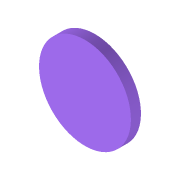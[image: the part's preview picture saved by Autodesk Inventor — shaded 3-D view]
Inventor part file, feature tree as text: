
AUTODESK INVENTOR PART (.ipt)
format: ipt  version: 2022 (Build 260153000, 153)  size: 123,392 bytes
history: native  units: mm
features: reference x6, other x3, revolve x1, sketch x1
ambient origin geometry x8: Origin, YZ Plane, XZ Plane, XY Plane, X Axis, Y Axis, Z Axis, Center Point
bodies: Volumenkörper1 (feature_tree)
feature tree (11):
  revolve  "Umdrehung1"
  sketch  "Skizze1"  dims[d0=12.0mm d1=0.2mm d2=6.1mm d3=3.0mm d4=360.0deg d5=0.2mm]
  reference  "Referenz1"
  reference  "Referenz2"
  reference  "Referenz3"
  reference  "Referenz4"
  reference  "Referenz5"
  reference  "Referenz6"
  other  "50_Assembly_ETL_Mould.iam"
  other  "50_ETL_Membrane_Mould_Lower_v0:1"
  other  "50_ETL_Membrane_v0:1"
